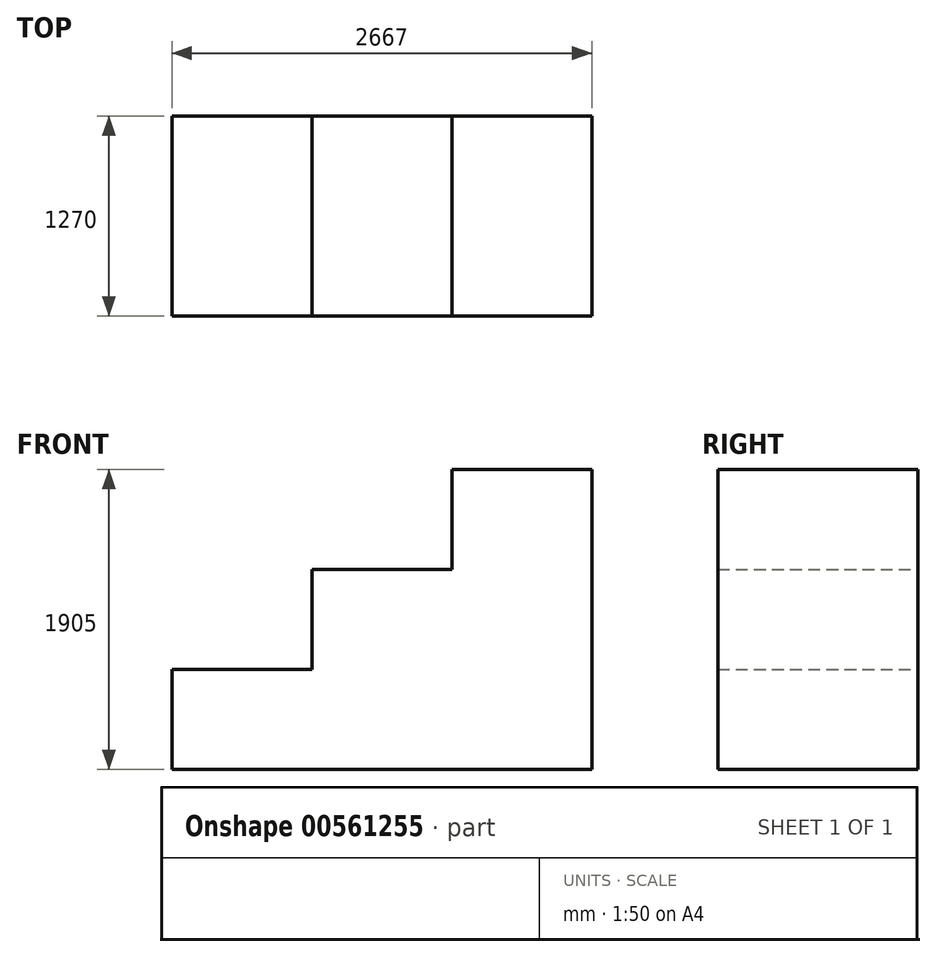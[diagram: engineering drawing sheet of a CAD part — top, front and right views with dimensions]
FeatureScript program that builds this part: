
annotation { "Feature Type Name" : "Feature", "Feature Type Description" : "" }
export const myFeature = defineFeature(function(context is Context, id is Id, definition is map)
    precondition{}
    {
        {
            var Q0;
            Q0=qCreatedBy(makeId("Front.planeOp"),FACE);
            var sketch = newSketch(context, id + "F0", { "sketchPlane" : qUnion([Q0])});
            skLineSegment(sketch, "E0.bottom", {"start": v(0, 0) * mm, "end": v(889, 0) * mm});
            skLineSegment(sketch, "E0.top", {"start": v(0, 1905) * mm, "end": v(889, 1905) * mm});
            skLineSegment(sketch, "E0.left", {"start": v(0, 0) * mm, "end": v(0, 1905) * mm});
            skLineSegment(sketch, "E0.right", {"start": v(889, 0) * mm, "end": v(889, 1905) * mm});
            skLineSegment(sketch, "E1.bottom", {"start": v(0, 0) * mm, "end": v(-889, 0) * mm});
            skLineSegment(sketch, "E1.top", {"start": v(0, 1270) * mm, "end": v(-889, 1270) * mm});
            skLineSegment(sketch, "E1.left", {"start": v(0, 0) * mm, "end": v(0, 1270) * mm});
            skLineSegment(sketch, "E1.right", {"start": v(-889, 0) * mm, "end": v(-889, 1270) * mm});
            skLineSegment(sketch, "E2.bottom", {"start": v(-889, 0) * mm, "end": v(-1778, 0) * mm});
            skLineSegment(sketch, "E2.top", {"start": v(-889, 635) * mm, "end": v(-1778, 635) * mm});
            skLineSegment(sketch, "E2.left", {"start": v(-889, 0) * mm, "end": v(-889, 635) * mm});
            skLineSegment(sketch, "E2.right", {"start": v(-1778, 0) * mm, "end": v(-1778, 635) * mm});
            skSolve(sketch);
        }
        {
            var Q0;
            Q0=makeQuery(id+"F0.imprint","IMPRINT",FACE,{"disambiguationData":[TD([[makeQuery(id+"F0.imprint","IMPRINT",EDGE,{"derivedFrom":sQuery(id+"F0.wireOp",EDGE,"E1.bottom")}),-1.0]])]});
            var Q1;
            Q1=makeQuery(id+"F0.imprint","IMPRINT",FACE,{"disambiguationData":[TD([[makeQuery(id+"F0.imprint","IMPRINT",EDGE,{"derivedFrom":sQuery(id+"F0.wireOp",EDGE,"E0.bottom")}),1.0]])]});
            var Q2;
            Q2=makeQuery(id+"F0.imprint","IMPRINT",FACE,{"disambiguationData":[TD([[makeQuery(id+"F0.imprint","IMPRINT",EDGE,{"derivedFrom":sQuery(id+"F0.wireOp",EDGE,"E2.bottom")}),-1.0]])]});
            extrude(context, id + "F1", {"entities" : qUnion([Q0, Q1, Q2]), "depth" : 1270 * mm, "offsetDistance" : 25.4 * mm});
        }
    });
